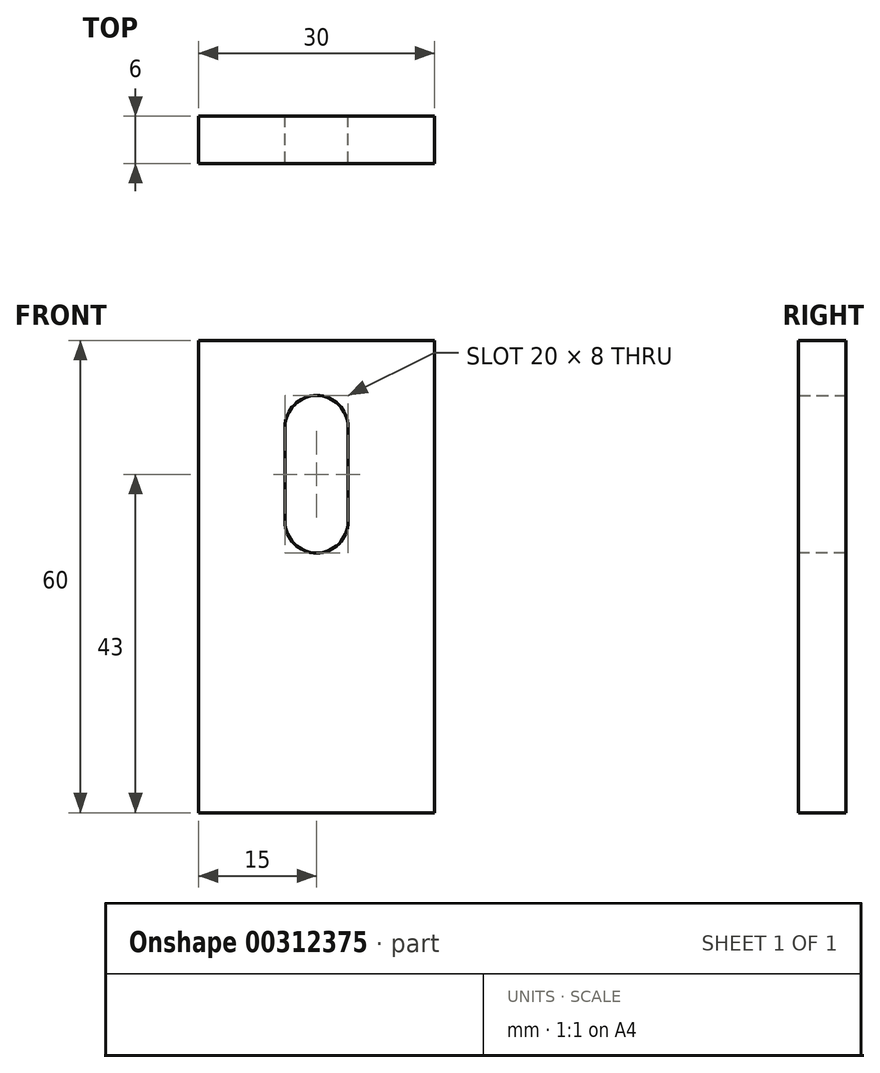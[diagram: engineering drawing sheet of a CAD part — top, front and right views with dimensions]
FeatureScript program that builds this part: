
annotation { "Feature Type Name" : "Feature", "Feature Type Description" : "" }
export const myFeature = defineFeature(function(context is Context, id is Id, definition is map)
    precondition{}
    {
        {
            var Q0;
            Q0=qCreatedBy(makeId("Front.planeOp"),FACE);
            var sketch = newSketch(context, id + "F0", { "sketchPlane" : qUnion([Q0])});
            skLineSegment(sketch, "E0.bottom", {"start": v(15, -30) * mm, "end": v(-15, -30) * mm});
            skLineSegment(sketch, "E0.top", {"start": v(15, 30) * mm, "end": v(-15, 30) * mm});
            skLineSegment(sketch, "E0.left", {"start": v(15, -30) * mm, "end": v(15, 30) * mm});
            skLineSegment(sketch, "E0.right", {"start": v(-15, -30) * mm, "end": v(-15, 30) * mm});
            skPoint(sketch, "E0.middle", {"position": v(0, 0) * mm});
            skLineSegment(sketch, "E1.bottom", {"start": v(4, 3) * mm, "end": v(-4, 3) * mm});
            skLineSegment(sketch, "E1.top", {"start": v(4, 23) * mm, "end": v(-4, 23) * mm});
            skLineSegment(sketch, "E1.left", {"start": v(4, 3) * mm, "end": v(4, 23) * mm});
            skLineSegment(sketch, "E1.right", {"start": v(-4, 3) * mm, "end": v(-4, 23) * mm});
            skPoint(sketch, "E1.middle", {"position": v(0, 13) * mm});
            skSolve(sketch);
        }
        {
            var Q0;
            Q0=makeQuery(id+"F0.imprint","IMPRINT",FACE,{"disambiguationData":[TD([[makeQuery(id+"F0.imprint","IMPRINT",EDGE,{"derivedFrom":sQuery(id+"F0.wireOp",EDGE,"E0.bottom")}),-1.0]])]});
            extrude(context, id + "F1", {"entities" : qUnion([Q0]), "depth" : 6 * mm});
        }
        {
            var Q0;
            Q0=makeQuery(id+"F1.opExtrude","SWEPT_EDGE",EDGE,{"disambiguationData":[OSD([sQuery(id+"F0.wireOp",EDGE,"E1.top"),sQuery(id+"F0.wireOp",EDGE,"E1.right")])]});
            var Q1;
            Q1=makeQuery(id+"F1.opExtrude","SWEPT_EDGE",EDGE,{"disambiguationData":[OSD([sQuery(id+"F0.wireOp",EDGE,"E1.top"),sQuery(id+"F0.wireOp",EDGE,"E1.left")])]});
            var Q2;
            Q2=makeQuery(id+"F1.opExtrude","SWEPT_EDGE",EDGE,{"disambiguationData":[OSD([sQuery(id+"F0.wireOp",EDGE,"E1.bottom"),sQuery(id+"F0.wireOp",EDGE,"E1.right")])]});
            var Q3;
            Q3=makeQuery(id+"F1.opExtrude","SWEPT_EDGE",EDGE,{"disambiguationData":[OSD([sQuery(id+"F0.wireOp",EDGE,"E1.bottom"),sQuery(id+"F0.wireOp",EDGE,"E1.left")])]});
            fillet(context, id + "F2", {"entities" : qUnion([Q0, Q1, Q2, Q3]), "radius" : 4 * mm, "tangentPropagation" : true, "allowEdgeOverflow" : false});
        }
    });
